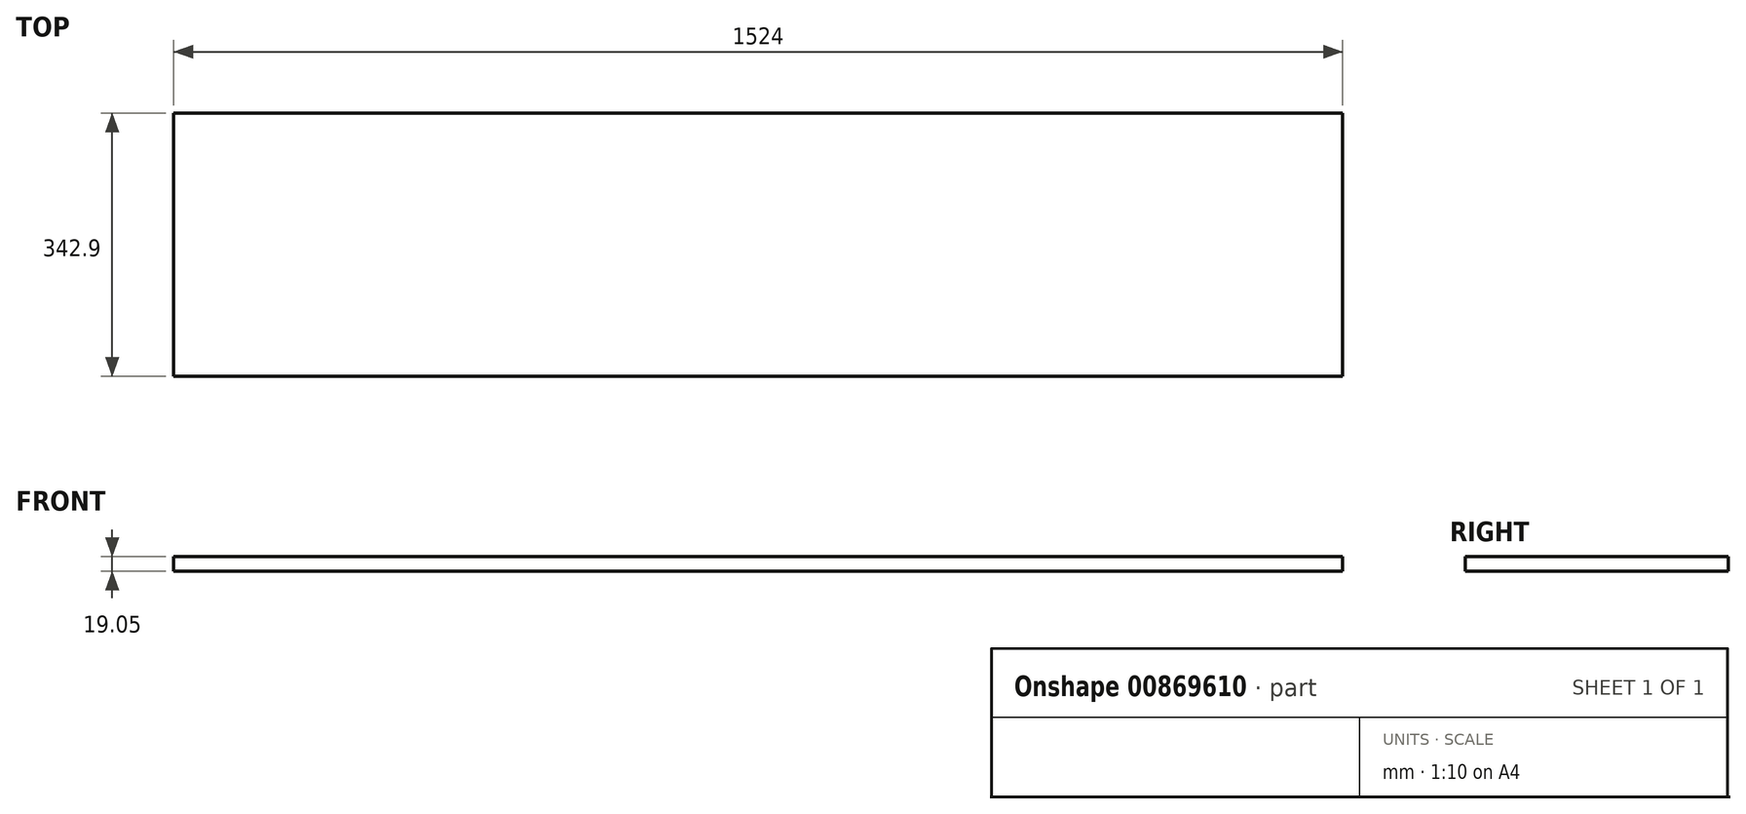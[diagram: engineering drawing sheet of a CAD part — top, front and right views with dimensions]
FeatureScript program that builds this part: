
annotation { "Feature Type Name" : "Feature", "Feature Type Description" : "" }
export const myFeature = defineFeature(function(context is Context, id is Id, definition is map)
    precondition{}
    {
        {
            var Q0;
            Q0=qCreatedBy(makeId("Top.planeOp"),FACE);
            var sketch = newSketch(context, id + "F0", { "sketchPlane" : qUnion([Q0])});
            skLineSegment(sketch, "E0.bottom", {"start": v(0, 0) * mm, "end": v(1524, 0) * mm});
            skLineSegment(sketch, "E0.top", {"start": v(0, -342.9) * mm, "end": v(1524, -342.9) * mm});
            skLineSegment(sketch, "E0.left", {"start": v(0, 0) * mm, "end": v(0, -342.9) * mm});
            skLineSegment(sketch, "E0.right", {"start": v(1524, 0) * mm, "end": v(1524, -342.9) * mm});
            skSolve(sketch);
        }
        {
            var Q0;
            Q0 = qSketchRegion(id + "F0", true);
            extrude(context, id + "F1", {"entities" : qUnion([Q0]), "depth" : 19.05 * mm, "offsetDistance" : 25.4 * mm});
        }
    });
